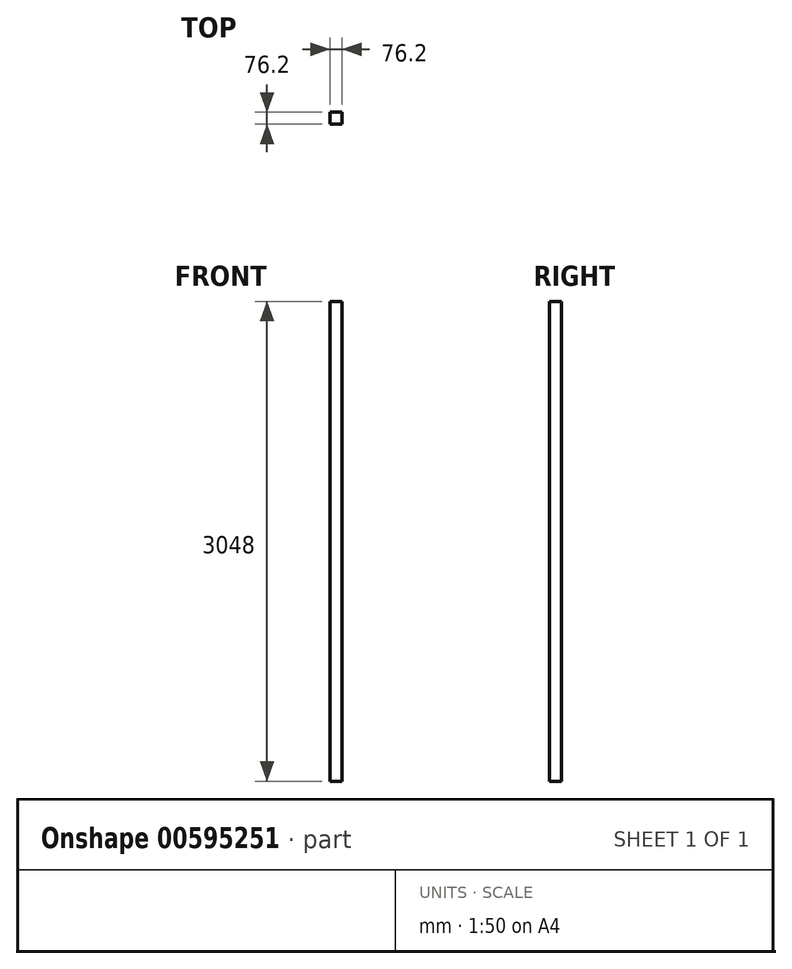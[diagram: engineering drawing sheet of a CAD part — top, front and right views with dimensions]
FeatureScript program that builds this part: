
annotation { "Feature Type Name" : "Feature", "Feature Type Description" : "" }
export const myFeature = defineFeature(function(context is Context, id is Id, definition is map)
    precondition{}
    {
        {
            var Q0;
            Q0=qCreatedBy(makeId("Right.planeOp"),FACE);
            var sketch = newSketch(context, id + "F0", { "sketchPlane" : qUnion([Q0])});
            skLineSegment(sketch, "E0.bottom", {"start": v(38.1, -1524) * mm, "end": v(-38.1, -1524) * mm});
            skLineSegment(sketch, "E0.top", {"start": v(38.1, 1524) * mm, "end": v(-38.1, 1524) * mm});
            skLineSegment(sketch, "E0.left", {"start": v(38.1, -1524) * mm, "end": v(38.1, 1524) * mm});
            skLineSegment(sketch, "E0.right", {"start": v(-38.1, -1524) * mm, "end": v(-38.1, 1524) * mm});
            skPoint(sketch, "E0.middle", {"position": v(0, 0) * mm});
            skSolve(sketch);
        }
        {
            var Q0;
            Q0=makeQuery(id+"F0.imprint","IMPRINT",FACE,{"disambiguationData":[TD([[makeQuery(id+"F0.imprint","IMPRINT",EDGE,{"derivedFrom":sQuery(id+"F0.wireOp",EDGE,"E0.bottom")}),-1.0]])]});
            extrude(context, id + "F1", {"entities" : qUnion([Q0]), "depth" : 76.2 * mm, "offsetDistance" : 25.4 * mm});
        }
    });
